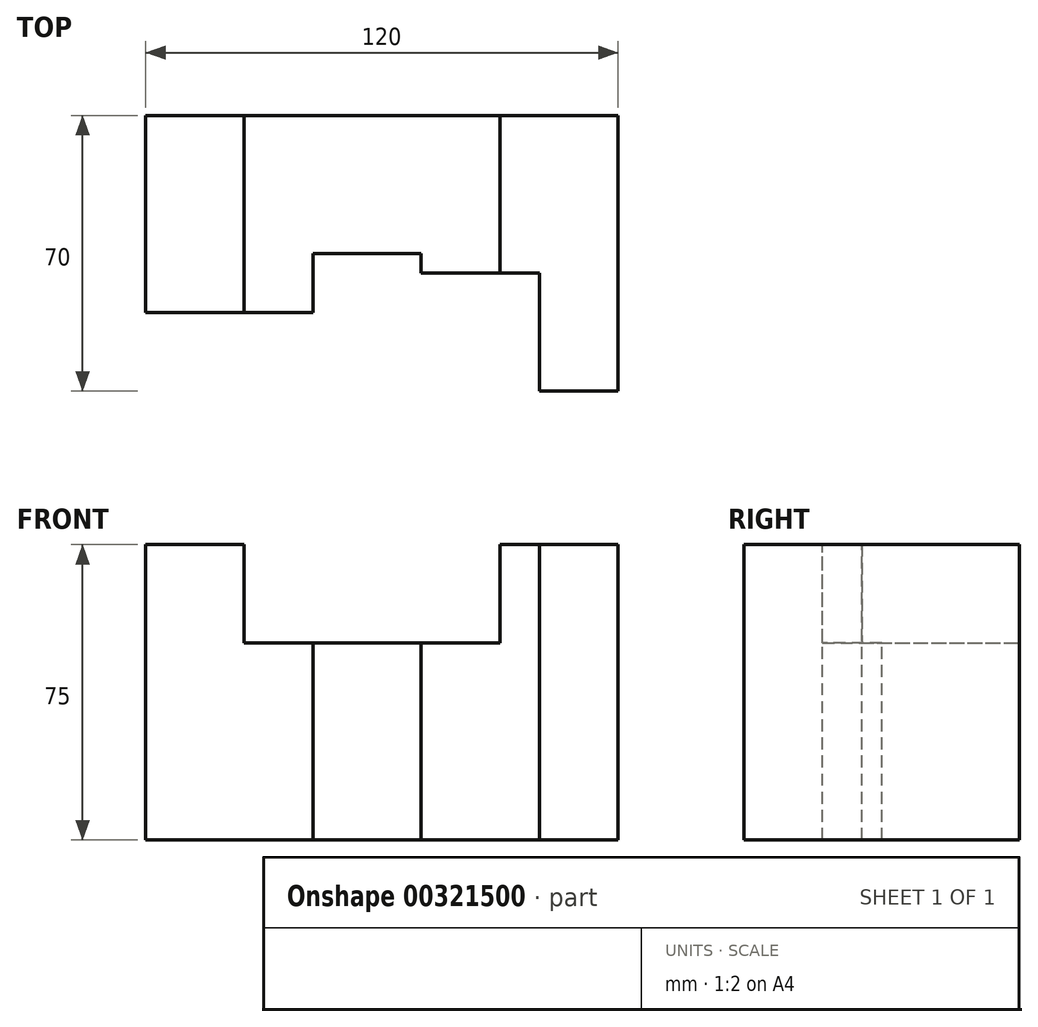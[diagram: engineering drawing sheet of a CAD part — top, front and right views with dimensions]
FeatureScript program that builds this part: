
annotation { "Feature Type Name" : "Feature", "Feature Type Description" : "" }
export const myFeature = defineFeature(function(context is Context, id is Id, definition is map)
    precondition{}
    {
        {
            var Q0;
            Q0=qCreatedBy(makeId("Front.planeOp"),FACE);
            var sketch = newSketch(context, id + "F0", { "sketchPlane" : qUnion([Q0])});
            skLineSegment(sketch, "E0", {"start": v(0, 0) * mm, "end": v(0, 75) * mm});
            skLineSegment(sketch, "E1", {"start": v(0, 75) * mm, "end": v(75, 75) * mm});
            skLineSegment(sketch, "E2", {"start": v(75, 75) * mm, "end": v(75, 0) * mm});
            skLineSegment(sketch, "E3", {"start": v(75, 0) * mm, "end": v(0, 0) * mm});
            skSolve(sketch);
        }
        {
            var Q0;
            Q0 = qSketchRegion(id + "F0", true);
            extrude(context, id + "F1", {"entities" : qUnion([Q0]), "endBound" : BoundingType.SYMMETRIC, "depth" : 70 * mm});
        }
        {
            var Q0;
            Q0=makeQuery(id+"F1.opExtrude","SWEPT_FACE",FACE,{"disambiguationData":[OSD([sQuery(id+"F0.wireOp",EDGE,"E1")])]});
            var sketch = newSketch(context, id + "F2", { "sketchPlane" : qUnion([Q0])});
            skLineSegment(sketch, "E4", {"start": v(0, 35) * mm, "end": v(0, -15) * mm});
            skLineSegment(sketch, "E5", {"start": v(0, -15) * mm, "end": v(17.5, -15) * mm});
            skLineSegment(sketch, "E6", {"start": v(17.5, -15) * mm, "end": v(17.5, 0) * mm});
            skLineSegment(sketch, "E7", {"start": v(17.5, 0) * mm, "end": v(45, 0) * mm});
            skLineSegment(sketch, "E8", {"start": v(45, 0) * mm, "end": v(45, -5) * mm});
            skLineSegment(sketch, "E9", {"start": v(45, -5) * mm, "end": v(75, -5) * mm});
            skLineSegment(sketch, "E10", {"start": v(0, 35) * mm, "end": v(75, 35) * mm});
            skLineSegment(sketch, "E11", {"start": v(75, 35) * mm, "end": v(75, -5) * mm});
            skSolve(sketch);
        }
        {
            var Q0;
            {var subQ0=sQuery(id+"F2.wireOp",EDGE,"E5");Q0=makeQuery(id+"F2.imprint","IMPRINT",FACE,{"disambiguationData":[TD([[makeQuery(id+"F2.imprint","IMPRINT",EDGE,{"derivedFrom":subQ0}),-1.0]])]});}
            extrude(context, id + "F3", {"entities" : qUnion([Q0]), "operationType" : NewBodyOperationType.REMOVE, "endBound" : BoundingType.THROUGH_ALL, "oppositeDirection" : true, "depth" : 25 * mm});
        }
        {
            var Q0;
            Q0=makeQuery(id+"F1.opExtrude","CAP_FACE",FACE,{"disambiguationData":[OSD([sQuery(id+"F0.wireOp",EDGE,"E0"),sQuery(id+"F0.wireOp",EDGE,"E1"),sQuery(id+"F0.wireOp",EDGE,"E2"),sQuery(id+"F0.wireOp",EDGE,"E3")])],"isStart":true});
            var sketch = newSketch(context, id + "F4", { "sketchPlane" : qUnion([Q0])});
            skLineSegment(sketch, "E12", {"start": v(0, 0) * mm, "end": v(0, 50) * mm});
            skLineSegment(sketch, "E13", {"start": v(0, 50) * mm, "end": v(-65, 50) * mm});
            skLineSegment(sketch, "E14", {"start": v(-65, 50) * mm, "end": v(-65, 75) * mm});
            skLineSegment(sketch, "E15", {"start": v(-65, 75) * mm, "end": v(-75, 75) * mm});
            skLineSegment(sketch, "E16", {"start": v(-75, 75) * mm, "end": v(-75, 0) * mm});
            skLineSegment(sketch, "E17", {"start": v(-75, 0) * mm, "end": v(0, 0) * mm});
            skSolve(sketch);
        }
        {
            var Q0;
            {var subQ0=sQuery(id+"F4.wireOp",EDGE,"E13");Q0=makeQuery(id+"F4.imprint","IMPRINT",FACE,{"disambiguationData":[TD([[makeQuery(id+"F4.imprint","IMPRINT",EDGE,{"derivedFrom":subQ0}),-1.0]])]});}
            extrude(context, id + "F5", {"entities" : qUnion([Q0]), "operationType" : NewBodyOperationType.REMOVE, "endBound" : BoundingType.THROUGH_ALL, "oppositeDirection" : true, "depth" : 25 * mm});
        }
        {
            var Q0;
            Q0=makeQuery(id+"F1.opExtrude","SWEPT_FACE",FACE,{"disambiguationData":[OSD([sQuery(id+"F0.wireOp",EDGE,"E0")])]});
            var sketch = newSketch(context, id + "F6", { "sketchPlane" : qUnion([Q0])});
            skLineSegment(sketch, "E18", {"start": v(-35, 0) * mm, "end": v(-35, 75) * mm});
            skLineSegment(sketch, "E19", {"start": v(-35, 75) * mm, "end": v(15, 75) * mm});
            skLineSegment(sketch, "E20", {"start": v(15, 75) * mm, "end": v(15, 0) * mm});
            skLineSegment(sketch, "E21", {"start": v(15, 0) * mm, "end": v(-35, 0) * mm});
            skSolve(sketch);
        }
        {
            var Q0;
            Q0 = qSketchRegion(id + "F6", true);
            extrude(context, id + "F7", {"entities" : qUnion([Q0]), "operationType" : NewBodyOperationType.ADD, "depth" : 25 * mm});
        }
        {
            var Q0;
            Q0=makeQuery(id+"F1.opExtrude","SWEPT_FACE",FACE,{"disambiguationData":[OSD([sQuery(id+"F0.wireOp",EDGE,"E2")])]});
            var sketch = newSketch(context, id + "F8", { "sketchPlane" : qUnion([Q0])});
            skLineSegment(sketch, "E22", {"start": v(35, 0) * mm, "end": v(-35, 0) * mm});
            skLineSegment(sketch, "E23", {"start": v(35, 0) * mm, "end": v(35, 75) * mm});
            skLineSegment(sketch, "E24", {"start": v(35, 75) * mm, "end": v(-35, 75) * mm});
            skLineSegment(sketch, "E25", {"start": v(-35, 75) * mm, "end": v(-35, 0) * mm});
            skSolve(sketch);
        }
        {
            var Q0;
            Q0 = qSketchRegion(id + "F8", true);
            extrude(context, id + "F9", {"entities" : qUnion([Q0]), "operationType" : NewBodyOperationType.ADD, "depth" : 20 * mm});
        }
    });
